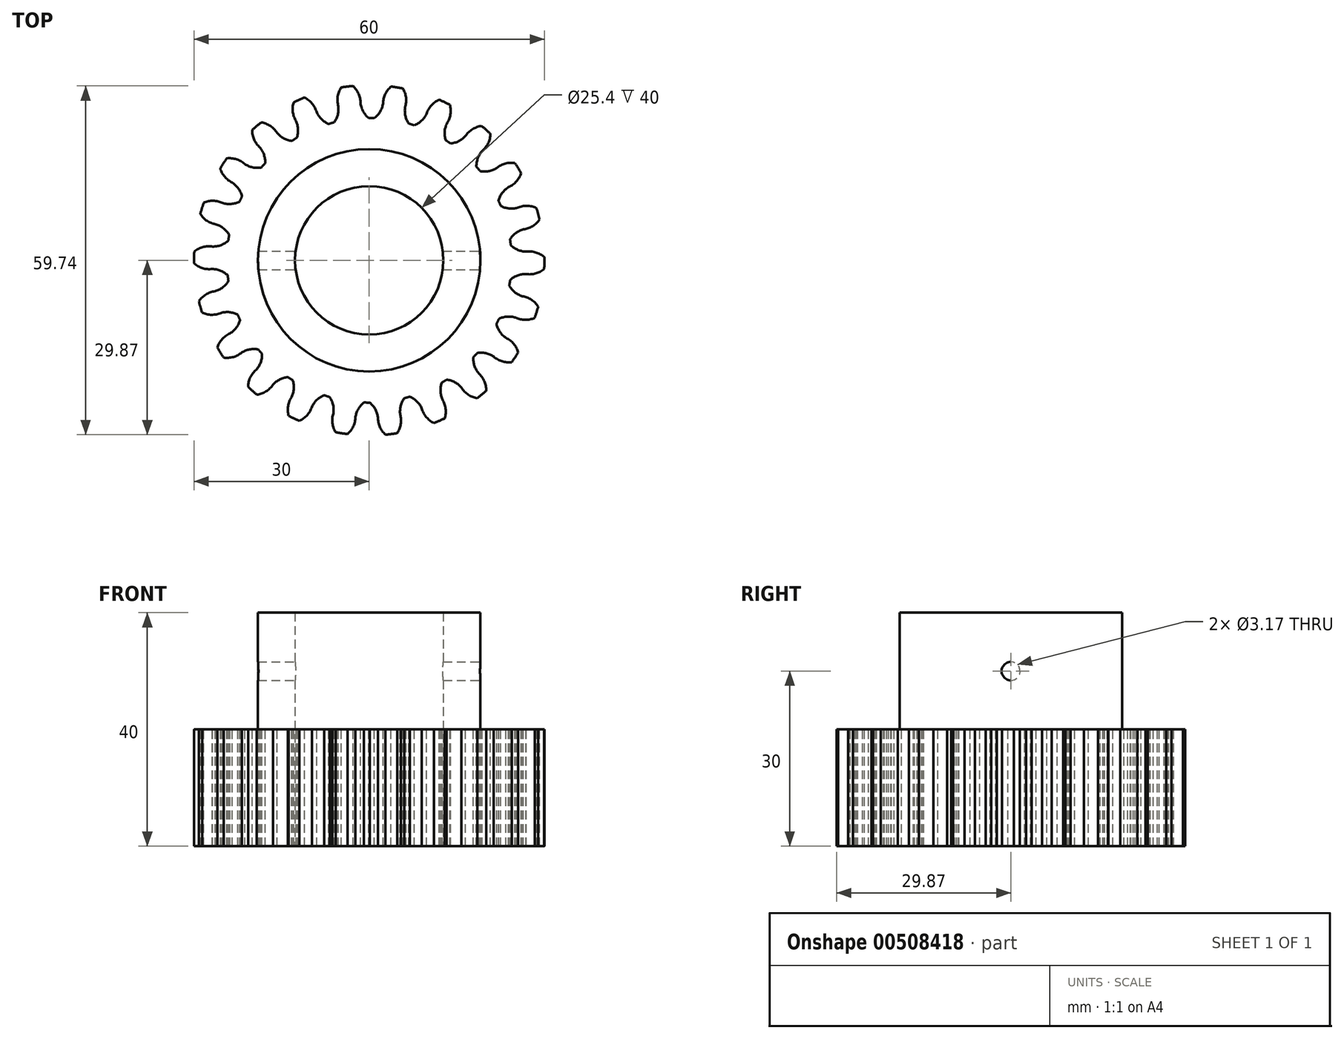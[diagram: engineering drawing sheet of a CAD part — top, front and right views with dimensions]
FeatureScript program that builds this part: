
annotation { "Feature Type Name" : "Feature", "Feature Type Description" : "" }
export const myFeature = defineFeature(function(context is Context, id is Id, definition is map)
    precondition{}
    {
        {
            var Q0;
            Q0=qCreatedBy(makeId("Top.planeOp"),FACE);
            var sketch = newSketch(context, id + "F0", { "sketchPlane" : qUnion([Q0])});
            skCircle(sketch, "E0", {"center": v(0, 0) * mm, "radius": 12.7 * mm});
            skCircle(sketch, "E1", {"center": v(0, 0) * mm, "radius": 30 * mm});
            skSolve(sketch);
        }
        {
            var Q0;
            Q0=makeQuery(id+"F0.imprint","IMPRINT",FACE,{"disambiguationData":[TD([[makeQuery(id+"F0.imprint","IMPRINT",EDGE,{"derivedFrom":sQuery(id+"F0.wireOp",EDGE,"E0")}),-1.0]])]});
            extrude(context, id + "F1", {"entities" : qUnion([Q0]), "offsetDistance" : 25 * mm, "depth" : 20 * mm});
        }
        {
            var Q0;
            Q0=makeQuery(id+"F1.opExtrude","CAP_FACE",FACE,{"disambiguationData":[OSD([sQuery(id+"F0.wireOp",EDGE,"E0"),sQuery(id+"F0.wireOp",EDGE,"E1")])],"isStart":false});
            var sketch = newSketch(context, id + "F2", { "sketchPlane" : qUnion([Q0])});
            skArc(sketch, "E2", {"start": v(3.74, 29.77) * mm, "mid": v(0.48, 30) * mm, "end": v(-2.78, 29.87) * mm});
            skArc(sketch, "E3", {"start": v(0.9, 24.36) * mm, "mid": v(0.4, 24.37) * mm, "end": v(-0.1, 24.37) * mm});
            skArc(sketch, "E4", {"start": v(-1.52, 27.46) * mm, "mid": v(-1.16, 25.76) * mm, "end": v(-0.1, 24.37) * mm});
            skArc(sketch, "E5.trimOffspring", {"start": v(0.9, 24.36) * mm, "mid": v(2, 25.7) * mm, "end": v(2.4, 27.4) * mm});
            skArc(sketch, "E6.trimOffspring", {"start": v(-1.5, 26.9) * mm, "mid": v(-1.81, 28.52) * mm, "end": v(-2.78, 29.87) * mm});
            skArc(sketch, "E7.trimOffspring", {"start": v(3.74, 29.77) * mm, "mid": v(2.73, 28.45) * mm, "end": v(2.36, 26.84) * mm});
            skSolve(sketch);
        }
        {
            var Q0;
            {var subQ7=sQuery(id+"F2.wireOp",EDGE,"E2");Q0=makeQuery(id+"F2.imprint","IMPRINT",FACE,{"disambiguationData":[TD([[makeQuery(id+"F2.imprint","IMPRINT",EDGE,{"derivedFrom":subQ7}),1.0]])]});}
            extrude(context, id + "F3", {"entities" : qUnion([Q0]), "operationType" : NewBodyOperationType.REMOVE, "oppositeDirection" : true, "offsetDistance" : 25 * mm, "depth" : 25 * mm});
        }
        {
            var Q0;
            Q0=makeQuery(id+"F3.boolean.opBoolean","COPY",FACE,{"derivedFrom":makeQuery(id+"F3.opExtrude","SWEPT_FACE",FACE,{"disambiguationData":[OSD([sQuery(id+"F2.wireOp",EDGE,"E6.trimOffspring")])]})});
            var Q1;
            Q1=makeQuery(id+"F3.boolean.opBoolean","COPY",FACE,{"derivedFrom":makeQuery(id+"F3.opExtrude","SWEPT_FACE",FACE,{"disambiguationData":[OSD([sQuery(id+"F2.wireOp",EDGE,"E4")])]})});
            var Q2;
            Q2=makeQuery(id+"F3.boolean.opBoolean","COPY",FACE,{"derivedFrom":makeQuery(id+"F3.opExtrude","SWEPT_FACE",FACE,{"disambiguationData":[OSD([sQuery(id+"F2.wireOp",EDGE,"E5.trimOffspring")])]})});
            var Q3;
            Q3=makeQuery(id+"F3.boolean.opBoolean","COPY",FACE,{"derivedFrom":makeQuery(id+"F3.opExtrude","SWEPT_FACE",FACE,{"disambiguationData":[OSD([sQuery(id+"F2.wireOp",EDGE,"E7.trimOffspring")])]})});
            var Q4;
            Q4=makeQuery(id+"F3.boolean.opBoolean","COPY",FACE,{"derivedFrom":makeQuery(id+"F3.opExtrude","SWEPT_FACE",FACE,{"disambiguationData":[OSD([sQuery(id+"F2.wireOp",EDGE,"E3")])]})});
            var Q5;
            Q5=makeQuery(id+"F1.opExtrude","CAP_EDGE",EDGE,{"disambiguationData":[OSD([sQuery(id+"F0.wireOp",EDGE,"E0")])],"isStart":false});
            circularPattern(context, id + "F4", {"patternType" : PatternType.FACE, "faces" : qUnion([Q0, Q1, Q2, Q3, Q4]), "axis" : qUnion([Q5]), "angle" : 360 * degree, "instanceCount" : 22, "equalSpace" : true});
        }
        {
            var Q0;
            Q0=makeQuery(id+"F1.opExtrude","CAP_FACE",FACE,{"disambiguationData":[OSD([sQuery(id+"F0.wireOp",EDGE,"E0"),sQuery(id+"F0.wireOp",EDGE,"E1")])],"isStart":false});
            var sketch = newSketch(context, id + "F5", { "sketchPlane" : qUnion([Q0])});
            skCircle(sketch, "E8", {"center": v(0, 0) * mm, "radius": 12.7 * mm});
            skCircle(sketch, "E9", {"center": v(0, 0) * mm, "radius": 19.05 * mm});
            skSolve(sketch);
        }
        {
            var Q0;
            Q0=makeQuery(id+"F5.imprint","IMPRINT",FACE,{"disambiguationData":[TD([[makeQuery(id+"F5.imprint","IMPRINT",EDGE,{"derivedFrom":sQuery(id+"F5.wireOp",EDGE,"E8")}),-1.0]])]});
            extrude(context, id + "F6", {"entities" : qUnion([Q0]), "operationType" : NewBodyOperationType.ADD, "depth" : 20 * mm});
        }
        {
            var Q0;
            Q0=qCreatedBy(makeId("Right.planeOp"),FACE);
            var sketch = newSketch(context, id + "F7", { "sketchPlane" : qUnion([Q0])});
            skCircle(sketch, "E10", {"center": v(0, 30) * mm, "radius": 1.59 * mm});
            skPoint(sketch, "E11", {"position": v(0, 40.01) * mm});
            skSolve(sketch);
        }
        {
            var Q0;
            Q0=makeQuery(id+"F7.imprint","IMPRINT",FACE,{"disambiguationData":[TD([[makeQuery(id+"F7.imprint","IMPRINT",EDGE,{"derivedFrom":sQuery(id+"F7.wireOp",EDGE,"E10")}),1.0]])]});
            var Q1;
            Q1=sQuery(id+"F7.wireOp",EDGE,"E10");
            extrude(context, id + "F8", {"entities" : qUnion([Q0]), "operationType" : NewBodyOperationType.REMOVE, "surfaceEntities" : qUnion([Q1]), "oppositeDirection" : true, "depth" : 25 * mm, "hasSecondDirection" : true, "secondDirectionOppositeDirection" : false, "secondDirectionDepth" : 25 * mm});
        }
    });
